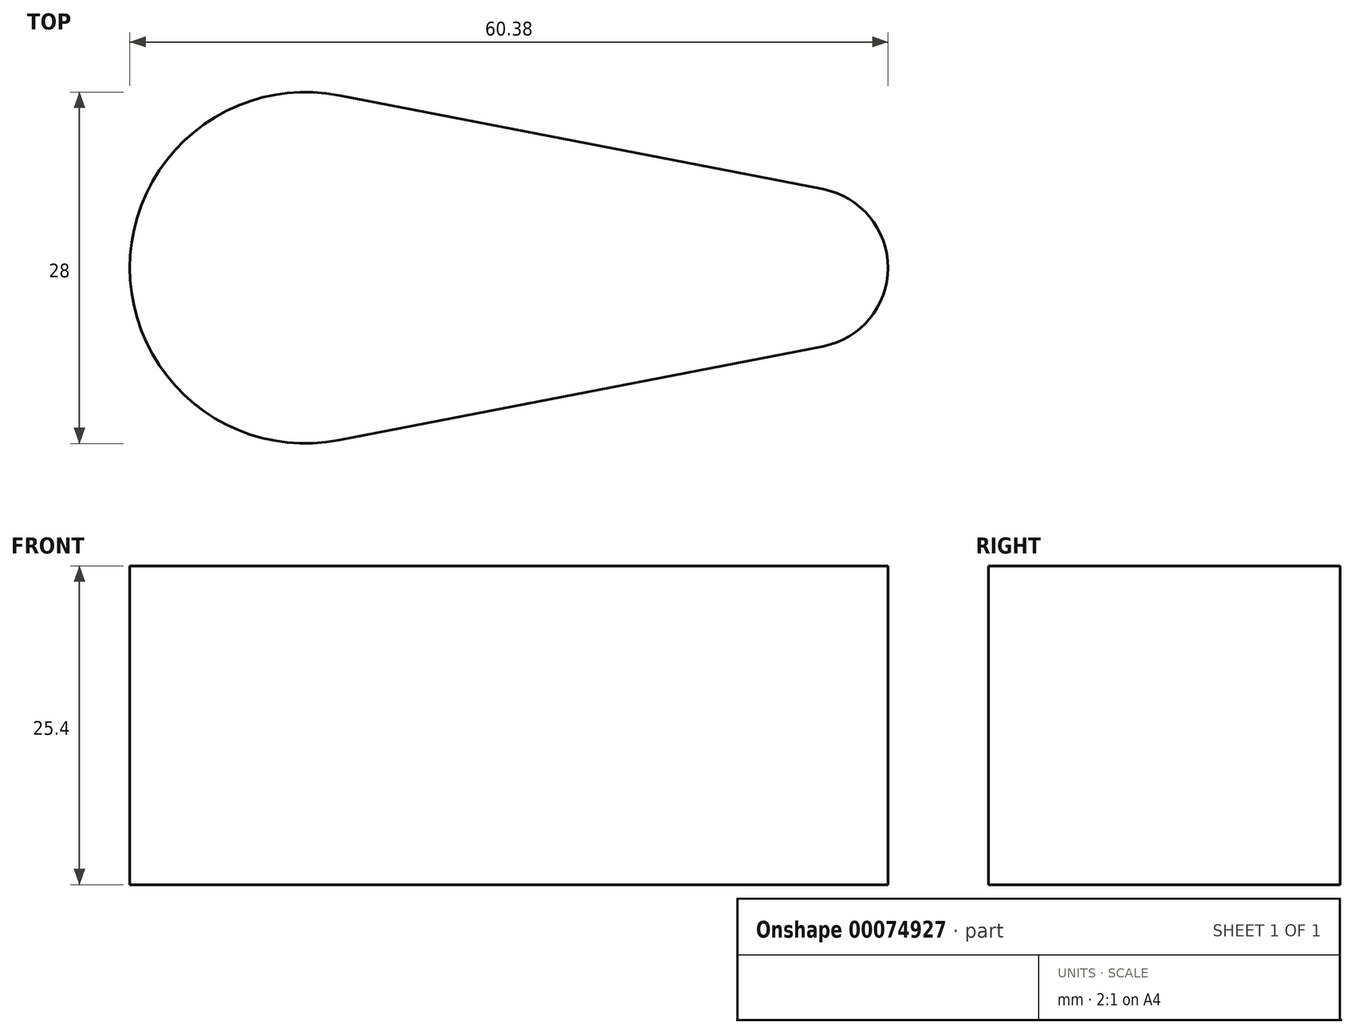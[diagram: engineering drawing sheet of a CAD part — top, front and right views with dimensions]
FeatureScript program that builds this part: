
annotation { "Feature Type Name" : "Feature", "Feature Type Description" : "" }
export const myFeature = defineFeature(function(context is Context, id is Id, definition is map)
    precondition{}
    {
        {
            var Q0;
            Q0=qCreatedBy(makeId("Top.planeOp"),FACE);
            var sketch = newSketch(context, id + "F0", { "sketchPlane" : qUnion([Q0])});
            skArc(sketch, "E0", {"start": v(2.67, 13.74) * mm, "mid": v(-14, 0) * mm, "end": v(2.67, -13.74) * mm});
            skArc(sketch, "E1", {"start": v(41.21, -6.26) * mm, "mid": v(46.38, 0) * mm, "end": v(41.21, 6.26) * mm});
            skLineSegment(sketch, "E2", {"start": v(2.67, -13.74) * mm, "end": v(41.21, -6.26) * mm});
            skLineSegment(sketch, "E3.MirrorCS", {"start": v(2.67, 13.74) * mm, "end": v(41.21, 6.26) * mm});
            skSolve(sketch);
        }
        {
            var Q0;
            {var subQ0=sQuery(id+"F0.wireOp",EDGE,"VaSxP7CY-8niV-tef4-DfrU-yQ5B6fyZiAdd");var subQ1=sQuery(id+"F0.wireOp",EDGE,"E0");var subQ2=makeQuery(id+"F0.imprint","INTERSECT",VERTEX,{"disambiguationData":[OD(0.0)],"derivedFrom":[subQ1,subQ0]});Q0=makeQuery(id+"F0.imprint","IMPRINT",FACE,{"disambiguationData":[TD([[makeQuery(id+"F0.imprint","IMPRINT",EDGE,{"disambiguationData":[TD([[subQ2,-1.0]])],"derivedFrom":subQ1}),1.0]])]});}
            var Q1;
            {var subQ0=sQuery(id+"F0.wireOp",EDGE,"VaSxP7CY-8niV-tef4-DfrU-yQ5B6fyZiAdd");var subQ1=sQuery(id+"F0.wireOp",EDGE,"E0");var subQ2=makeQuery(id+"F0.imprint","INTERSECT",VERTEX,{"disambiguationData":[OD(1.0)],"derivedFrom":[subQ1,subQ0]});Q1=makeQuery(id+"F0.imprint","IMPRINT",FACE,{"disambiguationData":[TD([[makeQuery(id+"F0.imprint","IMPRINT",EDGE,{"disambiguationData":[TD([[subQ2,1.0]])],"derivedFrom":subQ1}),-1.0]])]});}
            var Q2;
            {var subQ0=sQuery(id+"F0.wireOp",EDGE,"E1");var subQ1=makeQuery(id+"F0.imprint","INTERSECT",VERTEX,{"derivedFrom":[subQ0,sQuery(id+"F0.wireOp",EDGE,"VaSxP7CY-8niV-tef4-DfrU-yQ5B6fyZiAdd")]});Q2=makeQuery(id+"F0.imprint","IMPRINT",FACE,{"disambiguationData":[TD([[makeQuery(id+"F0.imprint","IMPRINT",EDGE,{"disambiguationData":[TD([[subQ1,-1.0]])],"derivedFrom":subQ0}),1.0]])]});}
            extrude(context, id + "F1", {"entities" : qUnion([Q0, Q1, Q2]), "depth" : 25.4 * mm});
        }
    });
